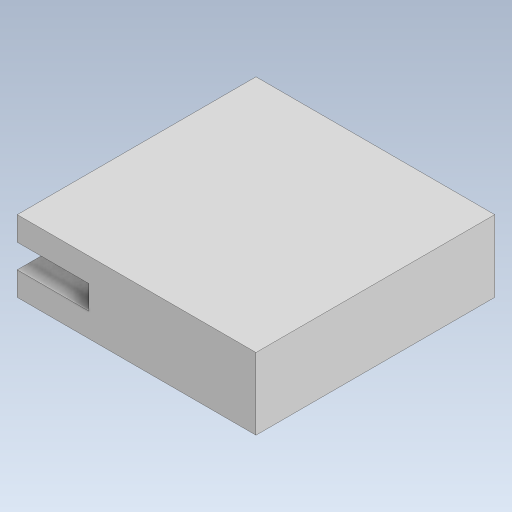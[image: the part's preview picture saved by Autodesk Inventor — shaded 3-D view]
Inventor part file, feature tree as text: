
AUTODESK INVENTOR PART (.ipt)
format: ipt  version: 2023.5 (Build 275446000, 446)  size: 269,312 bytes
history: native  units: in
note: dims shown in document units (in); Inventor stores cm internally (conversion verified against a paired STEP export)
features: extrude x3, sketch x3
ambient origin geometry x8: Origin, YZ Plane, XZ Plane, XY Plane, X Axis, Y Axis, Z Axis, Center Point
bodies: Solid1 (feature_tree)
feature tree (6):
  extrude  "Extrusion1"  Depth=0.7874in
  extrude  "Extrusion2"  Depth=0.2362in
  extrude  "Extrusion3"  Depth=0.0787in
  sketch  "Sketch1"  dims[d0=0.7874in d1=0.7874in]
  sketch  "Sketch2"  dims[d2=0.2362in d3=0.0in d4=0.2362in]
  sketch  "Sketch3"  dims[d5=0.0787in d6=0.0787in d7=0.1181in d8=0.0in d9=0.4331in d10=0.0787in d11=0.1181in d12=0.0in]
